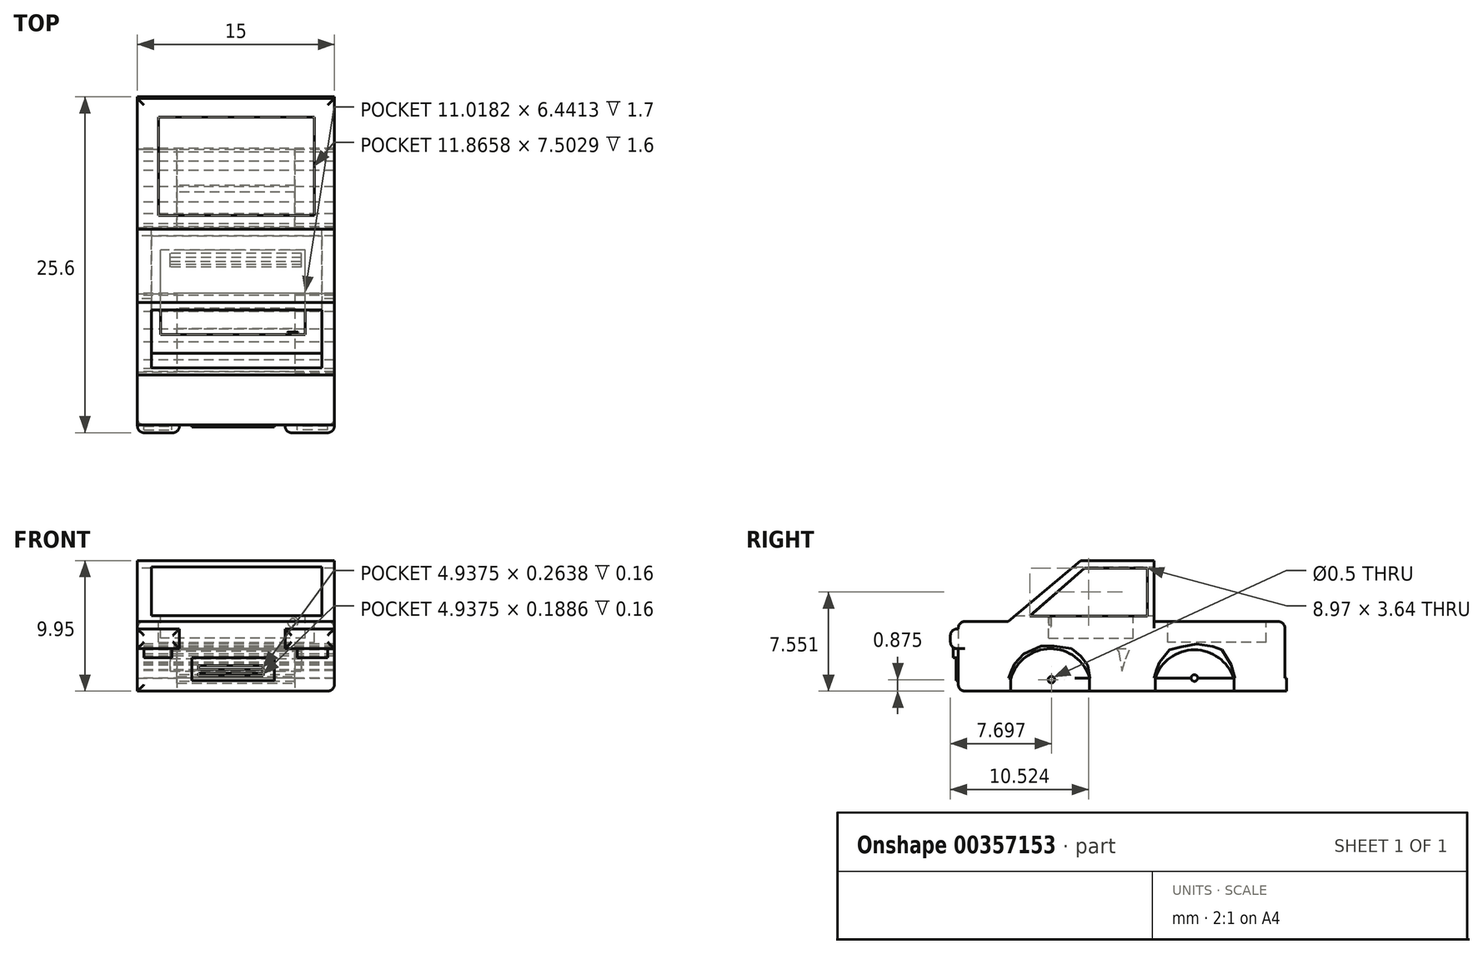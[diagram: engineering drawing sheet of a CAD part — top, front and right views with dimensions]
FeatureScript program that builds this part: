
annotation { "Feature Type Name" : "Feature", "Feature Type Description" : "" }
export const myFeature = defineFeature(function(context is Context, id is Id, definition is map)
    precondition{}
    {
        {
            var Q0;
            Q0=qCreatedBy(makeId("Top.planeOp"),FACE);
            var sketch = newSketch(context, id + "F0", { "sketchPlane" : qUnion([Q0])});
            skLineSegment(sketch, "E0.bottom", {"start": v(-7.5, -10.5) * mm, "end": v(7.5, -10.5) * mm});
            skLineSegment(sketch, "E0.top", {"start": v(-7.5, 10.5) * mm, "end": v(-4.5, 10.5) * mm});
            skLineSegment(sketch, "E0.left", {"start": v(-7.5, -10.5) * mm, "end": v(-7.5, -6.5) * mm});
            skLineSegment(sketch, "E0.right", {"start": v(7.5, -10.5) * mm, "end": v(7.5, -6.5) * mm});
            skPoint(sketch, "E0.middle", {"position": v(0, 0) * mm});
            skLineSegment(sketch, "E1", {"start": v(-7.5, 14.5) * mm, "end": v(-4.5, 14.5) * mm});
            skLineSegment(sketch, "E2", {"start": v(-4.5, 10.5) * mm, "end": v(-4.5, 4.5) * mm});
            skLineSegment(sketch, "E3", {"start": v(-4.5, 4.5) * mm, "end": v(-7.5, 4.5) * mm});
            skLineSegment(sketch, "E4", {"start": v(-7.5, 4.5) * mm, "end": v(-7.5, -0.5) * mm});
            skLineSegment(sketch, "E5", {"start": v(-7.5, -0.5) * mm, "end": v(-4.5, -0.5) * mm});
            skLineSegment(sketch, "E6", {"start": v(-4.5, -0.5) * mm, "end": v(-4.5, -6.5) * mm});
            skLineSegment(sketch, "E7", {"start": v(-4.5, -6.5) * mm, "end": v(-7.5, -6.5) * mm});
            skLineSegment(sketch, "E8.trimOffspring", {"start": v(-7.5, 10.5) * mm, "end": v(-7.5, 14.5) * mm});
            skLineSegment(sketch, "E9.trimOffspring", {"start": v(-7.5, -0.5) * mm, "end": v(-7.5, 4.5) * mm});
            skLineSegment(sketch, "E10", {"start": v(7.5, 14.5) * mm, "end": v(4.5, 14.5) * mm});
            skLineSegment(sketch, "E11", {"start": v(4.5, 10.5) * mm, "end": v(4.5, 4.5) * mm});
            skLineSegment(sketch, "E12", {"start": v(4.5, 4.5) * mm, "end": v(7.5, 4.5) * mm});
            skLineSegment(sketch, "E13", {"start": v(7.5, -0.5) * mm, "end": v(4.5, -0.5) * mm});
            skLineSegment(sketch, "E14", {"start": v(4.5, -0.5) * mm, "end": v(4.5, -6.5) * mm});
            skLineSegment(sketch, "E15", {"start": v(4.5, -6.5) * mm, "end": v(7.5, -6.5) * mm});
            skLineSegment(sketch, "E16.trimOffspring", {"start": v(7.5, -0.5) * mm, "end": v(7.5, 4.5) * mm});
            skLineSegment(sketch, "E17.trimOffspring", {"start": v(7.5, 10.5) * mm, "end": v(7.5, 14.5) * mm});
            skLineSegment(sketch, "E18", {"start": v(-4.5, 14.5) * mm, "end": v(4.5, 14.5) * mm});
            skLineSegment(sketch, "E19.trimOffspring", {"start": v(4.5, 10.5) * mm, "end": v(7.5, 10.5) * mm});
            skSolve(sketch);
        }
        {
            var Q0;
            Q0 = qSketchRegion(id + "F0", true);
            extrude(context, id + "F1", {"entities" : qUnion([Q0]), "depth" : 1 * mm});
        }
        {
            var Q0;
            Q0=qCreatedBy(makeId("Right.planeOp"),FACE);
            var sketch = newSketch(context, id + "F2", { "sketchPlane" : qUnion([Q0])});
            skArc(sketch, "E20", {"start": v(7, 0.38) * mm, "mid": v(5.53, 2.12) * mm, "end": v(4.02, 0.4) * mm});
            skLineSegment(sketch, "E21", {"start": v(4.02, 0.4) * mm, "end": v(7, 0.38) * mm});
            skSolve(sketch);
        }
        {
            var Q0;
            Q0 = qSketchRegion(id + "F2", true);
            extrude(context, id + "F3", {"entities" : qUnion([Q0]), "depth" : 25 * mm});
        }
        {
            var Q0;
            Q0 = qSketchRegion(id + "F2", true);
            extrude(context, id + "F4", {"entities" : qUnion([Q0]), "endBound" : BoundingType.SYMMETRIC, "depth" : 6 * mm});
        }
        {
            var Q0;
            Q0=makeQuery(id+"F3.opExtrude","SWEPT_BODY",BODY,{"disambiguationData":[OSD([sQuery(id+"F2.wireOp",EDGE,"E20"),sQuery(id+"F2.wireOp",EDGE,"E21")])]});
            deleteBodies(context, id + "F5", {"entities" : qUnion([Q0])});
        }
        {
            var Q0;
            Q0=makeQuery(id+"F4.opExtrude","SWEPT_BODY",BODY,{"disambiguationData":[OSD([sQuery(id+"F2.wireOp",EDGE,"E20"),sQuery(id+"F2.wireOp",EDGE,"E21")])]});
            deleteBodies(context, id + "F6", {"entities" : qUnion([Q0])});
        }
        {
            var Q0;
            Q0=qCreatedBy(makeId("Right.planeOp"),FACE);
            var sketch = newSketch(context, id + "F7", { "sketchPlane" : qUnion([Q0])});
            skArc(sketch, "E22", {"start": v(-0.47, 1) * mm, "mid": v(-3.49, 3.23) * mm, "end": v(-6.49, 0.98) * mm});
            skLineSegment(sketch, "E23", {"start": v(-0.47, 1) * mm, "end": v(-6.49, 0.98) * mm});
            skSolve(sketch);
        }
        {
            var Q0;
            Q0 = qSketchRegion(id + "F7", true);
            extrude(context, id + "F8", {"entities" : qUnion([Q0]), "endBound" : BoundingType.SYMMETRIC, "depth" : 9 * mm});
        }
        {
            var Q0;
            Q0 = qSketchRegion(id + "F7", true);
            extrude(context, id + "F9", {"entities" : qUnion([Q0]), "operationType" : NewBodyOperationType.ADD, "endBound" : BoundingType.SYMMETRIC, "depth" : 9 * mm});
        }
        {
            var Q0;
            Q0=qCreatedBy(makeId("Right.planeOp"),FACE);
            var sketch = newSketch(context, id + "F10", { "sketchPlane" : qUnion([Q0])});
            skArc(sketch, "E24", {"start": v(10.48, 1) * mm, "mid": v(7.5, 3.14) * mm, "end": v(4.5, 1) * mm});
            skLineSegment(sketch, "E25", {"start": v(4.5, 1) * mm, "end": v(10.48, 1) * mm});
            skSolve(sketch);
        }
        {
            var Q0;
            Q0 = qSketchRegion(id + "F10", true);
            extrude(context, id + "F11", {"entities" : qUnion([Q0]), "endBound" : BoundingType.SYMMETRIC, "depth" : 9 * mm});
        }
        {
            var Q0;
            Q0=makeQuery(id+"F11.opExtrude","CAP_FACE",FACE,{"disambiguationData":[OSD([sQuery(id+"F10.wireOp",EDGE,"E24"),sQuery(id+"F10.wireOp",EDGE,"E25")])],"isStart":true});
            var sketch = newSketch(context, id + "F12", { "sketchPlane" : qUnion([Q0])});
            skCircle(sketch, "E26", {"center": v(-7.5, 1) * mm, "radius": 0.25 * mm});
            skSolve(sketch);
        }
        {
            var Q0;
            Q0 = qSketchRegion(id + "F12", true);
            extrude(context, id + "F13", {"entities" : qUnion([Q0]), "operationType" : NewBodyOperationType.REMOVE, "endBound" : BoundingType.SYMMETRIC, "oppositeDirection" : true, "depth" : 25 * mm});
        }
        {
            var Q0;
            Q0=qCreatedBy(makeId("Right.planeOp"),FACE);
            var sketch = newSketch(context, id + "F14", { "sketchPlane" : qUnion([Q0])});
            skCircle(sketch, "E27", {"center": v(-3.4, 0.87) * mm, "radius": 0.25 * mm});
            skSolve(sketch);
        }
        {
            var Q0;
            Q0 = qSketchRegion(id + "F14", true);
            extrude(context, id + "F15", {"entities" : qUnion([Q0]), "operationType" : NewBodyOperationType.REMOVE, "endBound" : BoundingType.SYMMETRIC, "oppositeDirection" : true, "depth" : 25 * mm});
        }
        {
            var Q0;
            Q0=qCreatedBy(makeId("Right.planeOp"),FACE);
            var sketch = newSketch(context, id + "F16", { "sketchPlane" : qUnion([Q0])});
            skLineSegment(sketch, "E28", {"start": v(-10.5, 1) * mm, "end": v(-10.5, 5.3) * mm});
            skLineSegment(sketch, "E29", {"start": v(-10.5, 5.3) * mm, "end": v(-6.69, 5.3) * mm});
            skLineSegment(sketch, "E30", {"start": v(-6.69, 5.3) * mm, "end": v(-6.69, 0.97) * mm});
            skLineSegment(sketch, "E31", {"start": v(-0.46, 0.97) * mm, "end": v(-0.46, 5.3) * mm});
            skLineSegment(sketch, "E32", {"start": v(-0.46, 5.3) * mm, "end": v(-6.69, 5.3) * mm});
            skLineSegment(sketch, "E33", {"start": v(-0.46, 5.3) * mm, "end": v(4.42, 5.3) * mm});
            skLineSegment(sketch, "E34", {"start": v(4.42, 5.3) * mm, "end": v(4.42, 0.97) * mm});
            skLineSegment(sketch, "E35", {"start": v(10.59, 0.97) * mm, "end": v(10.59, 5.3) * mm});
            skLineSegment(sketch, "E36", {"start": v(10.59, 5.3) * mm, "end": v(4.42, 5.3) * mm});
            skLineSegment(sketch, "E37", {"start": v(10.59, 5.3) * mm, "end": v(14.38, 5.3) * mm});
            skLineSegment(sketch, "E38", {"start": v(14.38, 5.3) * mm, "end": v(14.38, 0.97) * mm});
            skLineSegment(sketch, "E39", {"start": v(14.38, 0.97) * mm, "end": v(10.59, 0.97) * mm});
            skLineSegment(sketch, "E40", {"start": v(4.42, 0.97) * mm, "end": v(-0.46, 0.97) * mm});
            skLineSegment(sketch, "E41", {"start": v(-10.5, 1) * mm, "end": v(-6.69, 0.97) * mm});
            skLineSegment(sketch, "E42", {"start": v(-6.69, 5.3) * mm, "end": v(-1.16, 9.95) * mm});
            skLineSegment(sketch, "E43", {"start": v(-1.16, 9.95) * mm, "end": v(4.42, 9.95) * mm});
            skLineSegment(sketch, "E44", {"start": v(4.42, 9.95) * mm, "end": v(4.42, 5.3) * mm});
            skLineSegment(sketch, "E45", {"start": v(3.9, 5.73) * mm, "end": v(3.9, 9.37) * mm});
            skLineSegment(sketch, "E46", {"start": v(3.9, 9.37) * mm, "end": v(-0.9, 9.37) * mm});
            skLineSegment(sketch, "E47", {"start": v(-0.9, 9.37) * mm, "end": v(-5.06, 5.73) * mm});
            skLineSegment(sketch, "E48", {"start": v(-5.06, 5.73) * mm, "end": v(3.9, 5.73) * mm});
            skLineSegment(sketch, "E49", {"start": v(4.42, 0.97) * mm, "end": v(4.6, 1.64) * mm});
            skLineSegment(sketch, "E50", {"start": v(4.6, 1.64) * mm, "end": v(4.84, 2.2) * mm});
            skLineSegment(sketch, "E51", {"start": v(4.84, 2.2) * mm, "end": v(5.58, 3.15) * mm});
            skLineSegment(sketch, "E52", {"start": v(5.58, 3.15) * mm, "end": v(6.47, 3.37) * mm});
            skLineSegment(sketch, "E53", {"start": v(6.47, 3.37) * mm, "end": v(7.66, 3.6) * mm});
            skLineSegment(sketch, "E54", {"start": v(7.66, 3.6) * mm, "end": v(8.89, 3.4) * mm});
            skLineSegment(sketch, "E55", {"start": v(8.89, 3.4) * mm, "end": v(9.6, 3.15) * mm});
            skLineSegment(sketch, "E56", {"start": v(9.6, 3.15) * mm, "end": v(10.3, 2.01) * mm});
            skLineSegment(sketch, "E57", {"start": v(10.3, 2.01) * mm, "end": v(10.59, 0.97) * mm});
            skLineSegment(sketch, "E58", {"start": v(-6.69, 0.97) * mm, "end": v(-6.43, 1.55) * mm});
            skLineSegment(sketch, "E59", {"start": v(-6.43, 1.55) * mm, "end": v(-6.23, 2.08) * mm});
            skLineSegment(sketch, "E60", {"start": v(-6.23, 2.08) * mm, "end": v(-5.54, 2.84) * mm});
            skLineSegment(sketch, "E61", {"start": v(-5.54, 2.84) * mm, "end": v(-4.2, 3.45) * mm});
            skLineSegment(sketch, "E62", {"start": v(-4.2, 3.45) * mm, "end": v(-3.2, 3.45) * mm});
            skLineSegment(sketch, "E63", {"start": v(-3.2, 3.45) * mm, "end": v(-1.86, 3.23) * mm});
            skLineSegment(sketch, "E64", {"start": v(-1.86, 3.23) * mm, "end": v(-1.18, 2.67) * mm});
            skLineSegment(sketch, "E65", {"start": v(-1.18, 2.67) * mm, "end": v(-0.64, 1.97) * mm});
            skLineSegment(sketch, "E66", {"start": v(-0.64, 1.97) * mm, "end": v(-0.46, 0.97) * mm});
            skSolve(sketch);
        }
        {
            var Q0;
            Q0 = qSketchRegion(id + "F16", true);
            extrude(context, id + "F17", {"entities" : qUnion([Q0]), "operationType" : NewBodyOperationType.ADD, "endBound" : BoundingType.SYMMETRIC, "depth" : 15 * mm});
        }
        {
            var Q0;
            Q0=makeQuery(id+"F17.opExtrude","SWEPT_FACE",FACE,{"disambiguationData":[OSD([sQuery(id+"F16.wireOp",EDGE,"E44")])]});
            shell(context, id + "F18", {"entities" : qUnion([Q0]), "thickness" : 2.5 * mm});
        }
        {
            var Q0;
            Q0=makeQuery(id+"F17.opExtrude","SWEPT_FACE",FACE,{"disambiguationData":[OSD([sQuery(id+"F16.wireOp",EDGE,"E44")])]});
            var sketch = newSketch(context, id + "F19", { "sketchPlane" : qUnion([Q0])});
            skLineSegment(sketch, "E67.bottom", {"start": v(-6.56, 9.46) * mm, "end": v(6.43, 9.46) * mm});
            skLineSegment(sketch, "E67.top", {"start": v(-6.56, 5.75) * mm, "end": v(6.43, 5.75) * mm});
            skLineSegment(sketch, "E67.left", {"start": v(-6.56, 9.46) * mm, "end": v(-6.56, 5.75) * mm});
            skLineSegment(sketch, "E67.right", {"start": v(6.43, 9.46) * mm, "end": v(6.43, 5.75) * mm});
            skSolve(sketch);
        }
        {
            var Q0;
            Q0 = qSketchRegion(id + "F19", true);
            extrude(context, id + "F20", {"entities" : qUnion([Q0]), "operationType" : NewBodyOperationType.REMOVE, "oppositeDirection" : true, "depth" : 25 * mm});
        }
        {
            var Q0;
            Q0=makeQuery(id+"F17.opExtrude","SWEPT_FACE",FACE,{"disambiguationData":[OSD([sQuery(id+"F16.wireOp",EDGE,"E48")])]});
            var sketch = newSketch(context, id + "F21", { "sketchPlane" : qUnion([Q0])});
            skLineSegment(sketch, "E68.bottom", {"start": v(5.28, -3.62) * mm, "end": v(-5.73, -3.62) * mm});
            skLineSegment(sketch, "E68.top", {"start": v(5.28, 2.82) * mm, "end": v(-5.73, 2.82) * mm});
            skLineSegment(sketch, "E68.left", {"start": v(5.28, -3.62) * mm, "end": v(5.28, 2.82) * mm});
            skLineSegment(sketch, "E68.right", {"start": v(-5.73, -3.62) * mm, "end": v(-5.73, 2.82) * mm});
            skSolve(sketch);
        }
        {
            var Q0;
            Q0 = qSketchRegion(id + "F21", true);
            extrude(context, id + "F22", {"entities" : qUnion([Q0]), "operationType" : NewBodyOperationType.REMOVE, "oppositeDirection" : true, "depth" : 1.7 * mm});
        }
        {
            var Q0;
            Q0=makeQuery(id+"F17.opExtrude","SWEPT_FACE",FACE,{"disambiguationData":[OSD([sQuery(id+"F16.wireOp",EDGE,"E36"),sQuery(id+"F16.wireOp",EDGE,"E37")])]});
            var sketch = newSketch(context, id + "F23", { "sketchPlane" : qUnion([Q0])});
            skLineSegment(sketch, "E69.bottom", {"start": v(-5.89, 12.97) * mm, "end": v(5.98, 12.97) * mm});
            skLineSegment(sketch, "E69.top", {"start": v(-5.89, 5.46) * mm, "end": v(5.98, 5.46) * mm});
            skLineSegment(sketch, "E69.left", {"start": v(-5.89, 12.97) * mm, "end": v(-5.89, 5.46) * mm});
            skLineSegment(sketch, "E69.right", {"start": v(5.98, 12.97) * mm, "end": v(5.98, 5.46) * mm});
            skSolve(sketch);
        }
        {
            var Q0;
            Q0 = qSketchRegion(id + "F23", true);
            extrude(context, id + "F24", {"entities" : qUnion([Q0]), "operationType" : NewBodyOperationType.REMOVE, "oppositeDirection" : true, "depth" : 1.6 * mm});
        }
        {
            var Q0;
            Q0=makeQuery(id+"F17.boolean.opBoolean","MERGE",FACE,{"derivedFrom":[makeQuery(id+"F1.opExtrude","SWEPT_FACE",FACE,{"disambiguationData":[OSD([sQuery(id+"F0.wireOp",EDGE,"E0.bottom")])]}),makeQuery(id+"F17.opExtrude","SWEPT_FACE",FACE,{"disambiguationData":[OSD([sQuery(id+"F16.wireOp",EDGE,"E28")])]})]});
            var sketch = newSketch(context, id + "F25", { "sketchPlane" : qUnion([Q0])});
            skLineSegment(sketch, "E70.bottom", {"start": v(-7.5, 4.74) * mm, "end": v(-4.3, 4.74) * mm});
            skLineSegment(sketch, "E70.top", {"start": v(-7.5, 3.24) * mm, "end": v(-4.3, 3.24) * mm});
            skLineSegment(sketch, "E70.left", {"start": v(-7.5, 4.74) * mm, "end": v(-7.5, 3.24) * mm});
            skLineSegment(sketch, "E70.right", {"start": v(-4.3, 4.74) * mm, "end": v(-4.3, 3.24) * mm});
            skLineSegment(sketch, "E71.bottom", {"start": v(7.5, 4.74) * mm, "end": v(3.74, 4.74) * mm});
            skLineSegment(sketch, "E71.top", {"start": v(7.5, 3.24) * mm, "end": v(3.74, 3.24) * mm});
            skLineSegment(sketch, "E71.left", {"start": v(7.5, 4.74) * mm, "end": v(7.5, 3.24) * mm});
            skLineSegment(sketch, "E71.right", {"start": v(3.74, 4.74) * mm, "end": v(3.74, 3.24) * mm});
            skSolve(sketch);
        }
        {
            var Q0;
            Q0 = qSketchRegion(id + "F25", true);
            extrude(context, id + "F26", {"entities" : qUnion([Q0]), "operationType" : NewBodyOperationType.ADD, "depth" : 0.6 * mm});
        }
        {
            var Q0;
            Q0=makeQuery(id+"F26.opExtrude","CAP_EDGE",EDGE,{"disambiguationData":[OSD([sQuery(id+"F25.wireOp",EDGE,"E70.bottom")])],"isStart":false});
            var Q1;
            Q1=makeQuery(id+"F26.opExtrude","CAP_EDGE",EDGE,{"disambiguationData":[OSD([sQuery(id+"F25.wireOp",EDGE,"E70.top")])],"isStart":false});
            var Q2;
            Q2=makeQuery(id+"F26.opExtrude","CAP_EDGE",EDGE,{"disambiguationData":[OSD([sQuery(id+"F25.wireOp",EDGE,"E70.left")])],"isStart":false});
            var Q3;
            Q3=makeQuery(id+"F26.opExtrude","CAP_EDGE",EDGE,{"disambiguationData":[OSD([sQuery(id+"F25.wireOp",EDGE,"E70.right")])],"isStart":false});
            var Q4;
            Q4=makeQuery(id+"F26.opExtrude","CAP_EDGE",EDGE,{"disambiguationData":[OSD([sQuery(id+"F25.wireOp",EDGE,"E71.right")])],"isStart":false});
            var Q5;
            Q5=makeQuery(id+"F26.opExtrude","CAP_EDGE",EDGE,{"disambiguationData":[OSD([sQuery(id+"F25.wireOp",EDGE,"E71.bottom")])],"isStart":false});
            var Q6;
            Q6=makeQuery(id+"F26.opExtrude","CAP_EDGE",EDGE,{"disambiguationData":[OSD([sQuery(id+"F25.wireOp",EDGE,"E71.top")])],"isStart":false});
            var Q7;
            Q7=makeQuery(id+"F26.opExtrude","CAP_EDGE",EDGE,{"disambiguationData":[OSD([sQuery(id+"F25.wireOp",EDGE,"E71.left")])],"isStart":false});
            var Q8;
            Q8=makeQuery(id+"F17.opExtrude","SWEPT_EDGE",EDGE,{"disambiguationData":[OSD([sQuery(id+"F16.wireOp",EDGE,"E28"),sQuery(id+"F16.wireOp",EDGE,"E29")])]});
            var Q9;
            {var subQ2=sQuery(id+"F0.wireOp",EDGE,"E0.right");var subQ3=sQuery(id+"F0.wireOp",EDGE,"E0.bottom");var subQ4=sQuery(id+"F16.wireOp",EDGE,"E28");Q9=makeQuery(id+"F26.boolean.opBoolean","SPLIT",EDGE,{"disambiguationData":[TD([makeQuery(id+"F26.opExtrude","SWEPT_FACE",FACE,{"disambiguationData":[OSD([sQuery(id+"F25.wireOp",EDGE,"E71.top")])]})])],"derivedFrom":makeQuery(id+"F17.boolean.opBoolean","MERGE",EDGE,{"derivedFrom":[makeQuery(id+"F1.opExtrude","SWEPT_EDGE",EDGE,{"disambiguationData":[OSD([subQ3,subQ2])]}),makeQuery(id+"F17.opExtrude","CAP_EDGE",EDGE,{"disambiguationData":[OSD([subQ4])],"isStart":false})]})});}
            var Q10;
            Q10=makeQuery(id+"F1.opExtrude","CAP_EDGE",EDGE,{"disambiguationData":[OSD([sQuery(id+"F0.wireOp",EDGE,"E0.bottom")])],"isStart":true});
            var Q11;
            {var subQ2=sQuery(id+"F0.wireOp",EDGE,"E0.left");var subQ3=sQuery(id+"F0.wireOp",EDGE,"E0.bottom");var subQ4=sQuery(id+"F16.wireOp",EDGE,"E28");Q11=makeQuery(id+"F26.boolean.opBoolean","SPLIT",EDGE,{"disambiguationData":[TD([makeQuery(id+"F26.opExtrude","SWEPT_FACE",FACE,{"disambiguationData":[OSD([sQuery(id+"F25.wireOp",EDGE,"E70.top")])]})])],"derivedFrom":makeQuery(id+"F17.boolean.opBoolean","MERGE",EDGE,{"derivedFrom":[makeQuery(id+"F1.opExtrude","SWEPT_EDGE",EDGE,{"disambiguationData":[OSD([subQ3,subQ2])]}),makeQuery(id+"F17.opExtrude","CAP_EDGE",EDGE,{"disambiguationData":[OSD([subQ4])],"isStart":true})]})});}
            var Q12;
            Q12=makeQuery(id+"F17.opExtrude","CAP_EDGE",EDGE,{"disambiguationData":[OSD([sQuery(id+"F16.wireOp",EDGE,"E36"),sQuery(id+"F16.wireOp",EDGE,"E37")])],"isStart":false});
            var Q13;
            Q13=makeQuery(id+"F17.opExtrude","SWEPT_EDGE",EDGE,{"disambiguationData":[OSD([sQuery(id+"F16.wireOp",EDGE,"E37"),sQuery(id+"F16.wireOp",EDGE,"E38")])]});
            var Q14;
            Q14=makeQuery(id+"F17.opExtrude","CAP_EDGE",EDGE,{"disambiguationData":[OSD([sQuery(id+"F16.wireOp",EDGE,"E36"),sQuery(id+"F16.wireOp",EDGE,"E37")])],"isStart":true});
            var Q15;
            Q15=makeQuery(id+"F1.opExtrude","CAP_EDGE",EDGE,{"disambiguationData":[OSD([sQuery(id+"F0.wireOp",EDGE,"E9.trimOffspring")])],"isStart":true});
            var Q16;
            Q16=makeQuery(id+"F1.opExtrude","CAP_EDGE",EDGE,{"disambiguationData":[OSD([sQuery(id+"F0.wireOp",EDGE,"E8.trimOffspring")])],"isStart":true});
            var Q17;
            Q17=makeQuery(id+"F1.opExtrude","CAP_EDGE",EDGE,{"disambiguationData":[OSD([sQuery(id+"F0.wireOp",EDGE,"E17.trimOffspring")])],"isStart":true});
            var Q18;
            Q18=makeQuery(id+"F1.opExtrude","CAP_EDGE",EDGE,{"disambiguationData":[OSD([sQuery(id+"F0.wireOp",EDGE,"E16.trimOffspring")])],"isStart":true});
            var Q19;
            Q19=makeQuery(id+"F1.opExtrude","CAP_EDGE",EDGE,{"disambiguationData":[OSD([sQuery(id+"F0.wireOp",EDGE,"E0.right")])],"isStart":true});
            fillet(context, id + "F27", {"entities" : qUnion([Q0, Q1, Q2, Q3, Q4, Q5, Q6, Q7, Q8, Q9, Q10, Q11, Q12, Q13, Q14, Q15, Q16, Q17, Q18, Q19]), "radius" : .5 * mm, "tangentPropagation" : true, "allowEdgeOverflow" : false});
        }
        {
            var Q0;
            Q0=makeQuery(id+"F17.boolean.opBoolean","MERGE",FACE,{"derivedFrom":[makeQuery(id+"F1.opExtrude","SWEPT_FACE",FACE,{"disambiguationData":[OSD([sQuery(id+"F0.wireOp",EDGE,"E0.bottom")])]}),makeQuery(id+"F17.opExtrude","SWEPT_FACE",FACE,{"disambiguationData":[OSD([sQuery(id+"F16.wireOp",EDGE,"E28")])]})]});
            var sketch = newSketch(context, id + "F28", { "sketchPlane" : qUnion([Q0])});
            skLineSegment(sketch, "E72.bottom", {"start": v(-7, 3.24) * mm, "end": v(-4.9, 3.24) * mm});
            skLineSegment(sketch, "E72.top", {"start": v(-7, 2.54) * mm, "end": v(-4.9, 2.54) * mm});
            skLineSegment(sketch, "E72.left", {"start": v(-7, 3.24) * mm, "end": v(-7, 2.54) * mm});
            skLineSegment(sketch, "E72.right", {"start": v(-4.9, 3.24) * mm, "end": v(-4.9, 2.54) * mm});
            skLineSegment(sketch, "E73.bottom", {"start": v(7, 3.24) * mm, "end": v(4.69, 3.24) * mm});
            skLineSegment(sketch, "E73.top", {"start": v(7, 2.54) * mm, "end": v(4.69, 2.54) * mm});
            skLineSegment(sketch, "E73.left", {"start": v(7, 3.24) * mm, "end": v(7, 2.54) * mm});
            skLineSegment(sketch, "E73.right", {"start": v(4.69, 3.24) * mm, "end": v(4.69, 2.54) * mm});
            skSolve(sketch);
        }
        {
            var Q0;
            Q0 = qSketchRegion(id + "F28", true);
            extrude(context, id + "F29", {"entities" : qUnion([Q0]), "operationType" : NewBodyOperationType.ADD, "depth" : 0.4 * mm});
        }
        {
            var Q0;
            Q0=makeQuery(id+"F17.boolean.opBoolean","MERGE",FACE,{"derivedFrom":[makeQuery(id+"F1.opExtrude","SWEPT_FACE",FACE,{"disambiguationData":[OSD([sQuery(id+"F0.wireOp",EDGE,"E0.bottom")])]}),makeQuery(id+"F17.opExtrude","SWEPT_FACE",FACE,{"disambiguationData":[OSD([sQuery(id+"F16.wireOp",EDGE,"E28")])]})]});
            var sketch = newSketch(context, id + "F30", { "sketchPlane" : qUnion([Q0])});
            skLineSegment(sketch, "E74.bottom", {"start": v(-3.34, 2.54) * mm, "end": v(2.93, 2.54) * mm});
            skLineSegment(sketch, "E74.top", {"start": v(-3.34, 0.79) * mm, "end": v(2.93, 0.79) * mm});
            skLineSegment(sketch, "E74.left", {"start": v(-3.34, 2.54) * mm, "end": v(-3.34, 0.79) * mm});
            skLineSegment(sketch, "E74.right", {"start": v(2.93, 2.54) * mm, "end": v(2.93, 0.79) * mm});
            skLineSegment(sketch, "E75", {"start": v(-3.34, 2.54) * mm, "end": v(-2.86, 2.54) * mm});
            skLineSegment(sketch, "E76", {"start": v(-2.86, 2.54) * mm, "end": v(-2.06, 2.54) * mm});
            skLineSegment(sketch, "E77", {"start": v(-2.06, 2.54) * mm, "end": v(-1.2, 2.54) * mm});
            skLineSegment(sketch, "E78", {"start": v(-1.2, 2.54) * mm, "end": v(-0.2, 2.54) * mm});
            skLineSegment(sketch, "E79", {"start": v(-0.2, 2.54) * mm, "end": v(0.6, 2.54) * mm});
            skLineSegment(sketch, "E80", {"start": v(0.6, 2.54) * mm, "end": v(1.27, 2.54) * mm});
            skLineSegment(sketch, "E81", {"start": v(1.27, 2.54) * mm, "end": v(2.08, 2.54) * mm});
            skLineSegment(sketch, "E82", {"start": v(2.08, 2.54) * mm, "end": v(2.93, 2.54) * mm});
            skLineSegment(sketch, "E83", {"start": v(2.08, 2.54) * mm, "end": v(2.08, 2.2) * mm});
            skLineSegment(sketch, "E84", {"start": v(2.08, 1.18) * mm, "end": v(2.08, 1.37) * mm});
            skLineSegment(sketch, "E85", {"start": v(1.27, 2.54) * mm, "end": v(1.27, 2.2) * mm});
            skLineSegment(sketch, "E86", {"start": v(0.6, 2.54) * mm, "end": v(0.6, 2.2) * mm});
            skLineSegment(sketch, "E87", {"start": v(-0.2, 2.54) * mm, "end": v(-0.2, 2.2) * mm});
            skLineSegment(sketch, "E88", {"start": v(-1.2, 2.54) * mm, "end": v(-1.2, 2.2) * mm});
            skLineSegment(sketch, "E89", {"start": v(-1.2, 1.18) * mm, "end": v(-1.2, 1.37) * mm});
            skLineSegment(sketch, "E90", {"start": v(-2.06, 2.54) * mm, "end": v(-2.06, 2.2) * mm});
            skLineSegment(sketch, "E91", {"start": v(-2.86, 2.54) * mm, "end": v(-2.86, 2.2) * mm});
            skLineSegment(sketch, "E92", {"start": v(-3.34, 1.66) * mm, "end": v(2.93, 1.66) * mm});
            skLineSegment(sketch, "E93", {"start": v(2.93, 1.66) * mm, "end": v(2.93, 2.2) * mm});
            skLineSegment(sketch, "E94", {"start": v(2.93, 2.2) * mm, "end": v(-3.34, 2.2) * mm});
            skLineSegment(sketch, "E95", {"start": v(-3.34, 2.2) * mm, "end": v(-3.34, 1.66) * mm});
            skLineSegment(sketch, "E96", {"start": v(2.93, 1.66) * mm, "end": v(2.93, 1.37) * mm});
            skLineSegment(sketch, "E97", {"start": v(2.93, 1.37) * mm, "end": v(-3.34, 1.37) * mm});
            skLineSegment(sketch, "E98", {"start": v(-3.34, 1.37) * mm, "end": v(-3.34, 1.18) * mm});
            skLineSegment(sketch, "E99", {"start": v(-3.34, 1.18) * mm, "end": v(2.93, 1.18) * mm});
            skLineSegment(sketch, "E100", {"start": v(2.93, 1.18) * mm, "end": v(2.93, 1.93) * mm});
            skLineSegment(sketch, "E101", {"start": v(2.93, 1.93) * mm, "end": v(-3.34, 1.93) * mm});
            skLineSegment(sketch, "E102.trimOffspring", {"start": v(-2.86, 1.93) * mm, "end": v(-2.86, 1.66) * mm});
            skLineSegment(sketch, "E103.trimOffspring", {"start": v(-2.06, 1.93) * mm, "end": v(-2.06, 1.66) * mm});
            skLineSegment(sketch, "E104.trimOffspring", {"start": v(-1.2, 2.2) * mm, "end": v(-1.2, 2.54) * mm});
            skLineSegment(sketch, "E105.trimOffspring", {"start": v(-0.2, 1.93) * mm, "end": v(-0.2, 1.66) * mm});
            skLineSegment(sketch, "E106.trimOffspring", {"start": v(0.6, 1.93) * mm, "end": v(0.6, 1.66) * mm});
            skLineSegment(sketch, "E107.trimOffspring", {"start": v(-1.2, 1.93) * mm, "end": v(-1.2, 1.18) * mm});
            skLineSegment(sketch, "E108.trimOffspring", {"start": v(1.27, 1.93) * mm, "end": v(1.27, 1.66) * mm});
            skLineSegment(sketch, "E109.trimOffspring", {"start": v(2.08, 1.93) * mm, "end": v(2.08, 1.66) * mm});
            skLineSegment(sketch, "E110.trimOffspring", {"start": v(2.08, 1.37) * mm, "end": v(2.08, 1.18) * mm});
            skLineSegment(sketch, "E111.trimOffspring", {"start": v(2.08, 2.2) * mm, "end": v(2.08, 2.54) * mm});
            skLineSegment(sketch, "E112.trimOffspring", {"start": v(2.08, 1.66) * mm, "end": v(2.08, 1.93) * mm});
            skLineSegment(sketch, "E113.trimOffspring", {"start": v(1.27, 1.37) * mm, "end": v(1.27, 1.18) * mm});
            skLineSegment(sketch, "E114.trimOffspring", {"start": v(0.6, 1.37) * mm, "end": v(0.6, 1.18) * mm});
            skLineSegment(sketch, "E115.trimOffspring", {"start": v(-0.2, 1.37) * mm, "end": v(-0.2, 1.18) * mm});
            skLineSegment(sketch, "E116.trimOffspring", {"start": v(-1.2, 1.66) * mm, "end": v(-1.2, 1.93) * mm});
            skLineSegment(sketch, "E117.trimOffspring", {"start": v(-2.06, 1.37) * mm, "end": v(-2.06, 1.18) * mm});
            skLineSegment(sketch, "E118.trimOffspring", {"start": v(-2.86, 1.37) * mm, "end": v(-2.86, 1.18) * mm});
            skPoint(sketch, "E119.orphan", {"position": v(-0.2, 0.79) * mm});
            skSolve(sketch);
        }
        {
            var Q0;
            Q0 = qSketchRegion(id + "F30", true);
            extrude(context, id + "F31", {"entities" : qUnion([Q0]), "operationType" : NewBodyOperationType.ADD, "depth" : 0.16 * mm});
        }
        {
            var Q0;
            Q0=makeQuery(id+"F22.boolean.opBoolean","COPY",FACE,{"derivedFrom":makeQuery(id+"F22.opExtrude","SWEPT_FACE",FACE,{"disambiguationData":[OSD([sQuery(id+"F21.wireOp",EDGE,"E68.bottom")])]})});
            var sketch = newSketch(context, id + "F32", { "sketchPlane" : qUnion([Q0])});
            skCircle(sketch, "E120", {"center": v(-4.34, 5.27) * mm, "radius": 0.25 * mm});
            skSolve(sketch);
        }
        {
            var Q0;
            Q0 = qSketchRegion(id + "F32", true);
            extrude(context, id + "F33", {"entities" : qUnion([Q0]), "operationType" : NewBodyOperationType.ADD, "depth" : 0.17 * mm});
        }
        {
            var Q0;
            Q0=makeQuery(id+"F33.opExtrude","CAP_FACE",FACE,{"disambiguationData":[OSD([sQuery(id+"F32.wireOp",EDGE,"E120")])],"isStart":false});
            var sketch = newSketch(context, id + "F34", { "sketchPlane" : qUnion([Q0])});
            skCircle(sketch, "E121", {"center": v(-4.34, 5.27) * mm, "radius": 0.4 * mm});
            skSolve(sketch);
        }
        {
            var Q0;
            Q0 = qSketchRegion(id + "F34", true);
            extrude(context, id + "F35", {"entities" : qUnion([Q0]), "operationType" : NewBodyOperationType.ADD, "depth" : 0.02 * mm});
        }
    });
